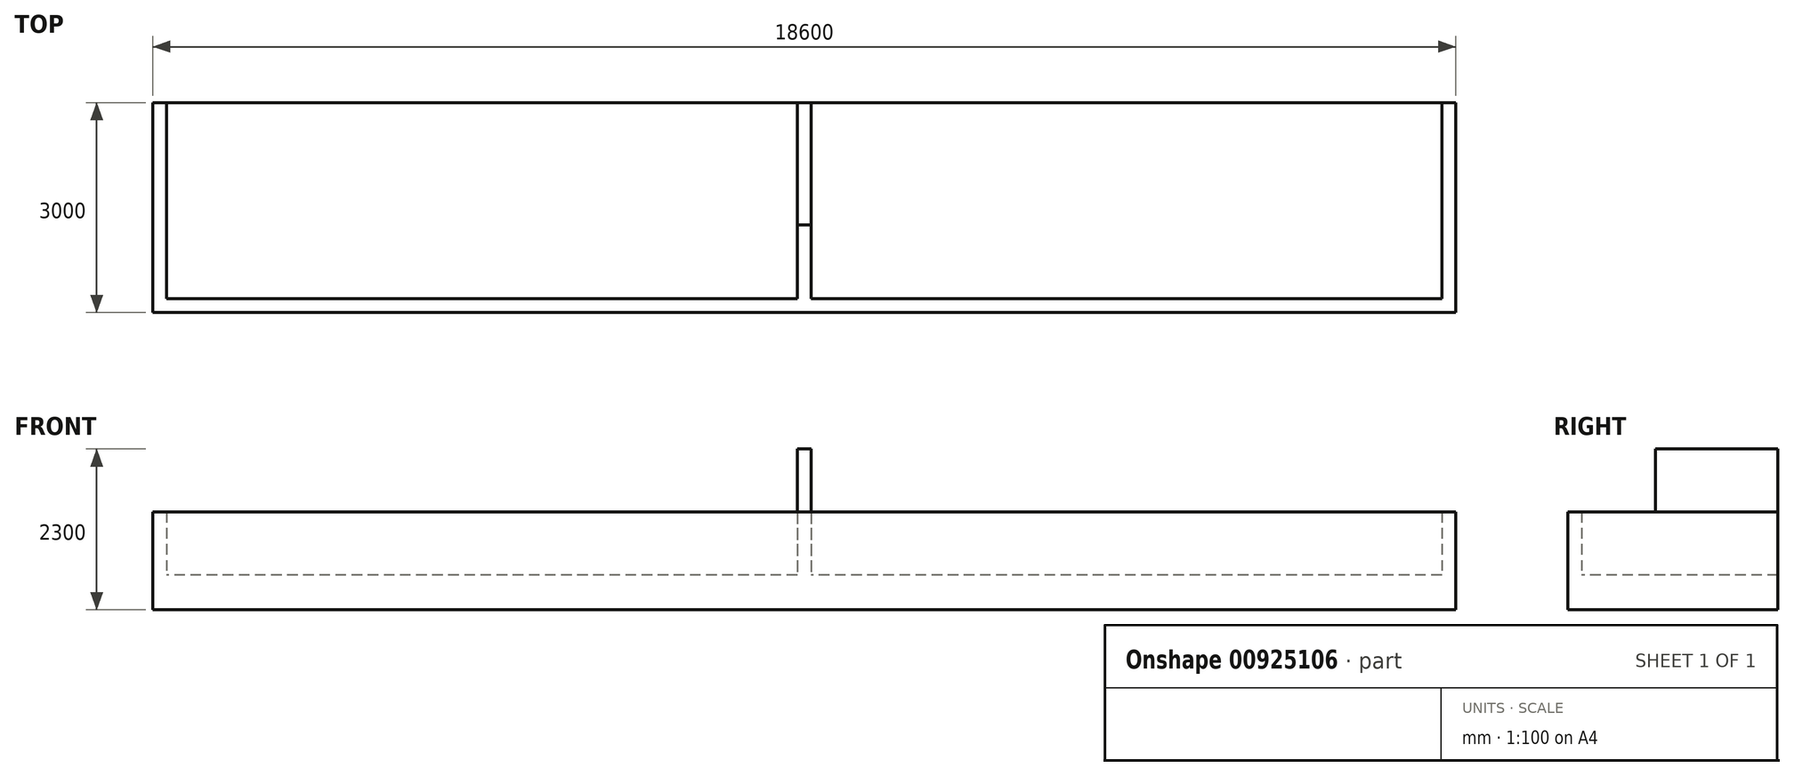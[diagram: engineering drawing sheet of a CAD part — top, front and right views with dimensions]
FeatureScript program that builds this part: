
annotation { "Feature Type Name" : "Feature", "Feature Type Description" : "" }
export const myFeature = defineFeature(function(context is Context, id is Id, definition is map)
    precondition{}
    {
        {
            var Q0;
            Q0=qCreatedBy(makeId("Top.planeOp"),FACE);
            var sketch = newSketch(context, id + "F0", { "sketchPlane" : qUnion([Q0])});
            skLineSegment(sketch, "E0.bottom", {"start": v(9300, 1500) * mm, "end": v(-9300, 1500) * mm});
            skLineSegment(sketch, "E0.top", {"start": v(9300, -1500) * mm, "end": v(-9300, -1500) * mm});
            skLineSegment(sketch, "E0.left", {"start": v(9300, 1500) * mm, "end": v(9300, -1500) * mm});
            skLineSegment(sketch, "E0.right", {"start": v(-9300, 1500) * mm, "end": v(-9300, -1500) * mm});
            skPoint(sketch, "E0.middle", {"position": v(0, 0) * mm});
            skLineSegment(sketch, "E1.bottom", {"start": v(-100, 1500) * mm, "end": v(100, 1500) * mm});
            skLineSegment(sketch, "E1.top", {"start": v(-100, -1500) * mm, "end": v(100, -1500) * mm});
            skLineSegment(sketch, "E1.left", {"start": v(-100, 1500) * mm, "end": v(-100, -1500) * mm});
            skLineSegment(sketch, "E1.right", {"start": v(100, 1500) * mm, "end": v(100, -1500) * mm});
            skLineSegment(sketch, "E2.top", {"start": v(-100, -250) * mm, "end": v(100, -250) * mm});
            skLineSegment(sketch, "E2.left", {"start": v(-100, -1500) * mm, "end": v(-100, -250) * mm});
            skLineSegment(sketch, "E2.right", {"start": v(100, -1500) * mm, "end": v(100, -250) * mm});
            skLineSegment(sketch, "E3.bottom", {"start": v(-9300, 1500) * mm, "end": v(-9100, 1500) * mm});
            skLineSegment(sketch, "E3.top", {"start": v(-9300, -1500) * mm, "end": v(-9100, -1500) * mm});
            skLineSegment(sketch, "E3.right", {"start": v(-9100, 1500) * mm, "end": v(-9100, -1500) * mm});
            skLineSegment(sketch, "E4.bottom", {"start": v(9300, 1500) * mm, "end": v(9100, 1500) * mm});
            skLineSegment(sketch, "E4.top", {"start": v(9300, -1500) * mm, "end": v(9100, -1500) * mm});
            skLineSegment(sketch, "E4.right", {"start": v(9100, 1500) * mm, "end": v(9100, -1500) * mm});
            skLineSegment(sketch, "E5.bottom", {"start": v(9100, -1500) * mm, "end": v(-9100, -1500) * mm});
            skLineSegment(sketch, "E5.top", {"start": v(9100, -1300) * mm, "end": v(-9100, -1300) * mm});
            skLineSegment(sketch, "E5.left", {"start": v(9100, -1500) * mm, "end": v(9100, -1300) * mm});
            skLineSegment(sketch, "E5.right", {"start": v(-9100, -1500) * mm, "end": v(-9100, -1300) * mm});
            skSolve(sketch);
        }
        {
            var Q0;
            {var subQ1=sQuery(id+"F0.wireOp",EDGE,"E0.bottom");var subQ5=sQuery(id+"F0.wireOp",EDGE,"E1.left");var subQ8=makeQuery(id+"F0.imprint","INTERSECT",VERTEX,{"derivedFrom":[subQ1,subQ5]});Q0=makeQuery(id+"F0.imprint","IMPRINT",FACE,{"disambiguationData":[TD([[makeQuery(id+"F0.imprint","IMPRINT",EDGE,{"disambiguationData":[TD([[subQ8,-1.0]])],"derivedFrom":subQ1}),1.0]])]});}
            var Q1;
            {var subQ0=sQuery(id+"F0.wireOp",EDGE,"E4.right");var subQ1=sQuery(id+"F0.wireOp",EDGE,"E0.bottom");var subQ2=makeQuery(id+"F0.imprint","INTERSECT",VERTEX,{"derivedFrom":[subQ1,subQ0]});Q1=makeQuery(id+"F0.imprint","IMPRINT",FACE,{"disambiguationData":[TD([[makeQuery(id+"F0.imprint","IMPRINT",EDGE,{"disambiguationData":[TD([[subQ2,-1.0]])],"derivedFrom":subQ1}),1.0]])]});}
            extrude(context, id + "F1", {"entities" : qUnion([Q0, Q1]), "depth" : 500 * mm, "offsetDistance" : 25 * mm});
        }
        {
            var Q0;
            {var subQ0=sQuery(id+"F0.wireOp",EDGE,"E0.right");Q0=makeQuery(id+"F0.imprint","IMPRINT",FACE,{"disambiguationData":[TD([[makeQuery(id+"F0.imprint","IMPRINT",EDGE,{"derivedFrom":subQ0}),1.0]])]});}
            var Q1;
            {var subQ0=sQuery(id+"F0.wireOp",EDGE,"E1.left");var subQ1=sQuery(id+"F0.wireOp",EDGE,"E0.top");var subQ2=makeQuery(id+"F0.imprint","INTERSECT",VERTEX,{"derivedFrom":[subQ1,subQ0]});Q1=makeQuery(id+"F0.imprint","IMPRINT",FACE,{"disambiguationData":[TD([[makeQuery(id+"F0.imprint","IMPRINT",EDGE,{"disambiguationData":[TD([[subQ2,-1.0]])],"derivedFrom":subQ1}),-1.0]])]});}
            var Q2;
            {var subQ4=sQuery(id+"F0.wireOp",EDGE,"E0.left");Q2=makeQuery(id+"F0.imprint","IMPRINT",FACE,{"disambiguationData":[TD([[makeQuery(id+"F0.imprint","IMPRINT",EDGE,{"derivedFrom":subQ4}),-1.0]])]});}
            var Q3;
            {var subQ0=sQuery(id+"F0.wireOp",EDGE,"E4.right");var subQ1=sQuery(id+"F0.wireOp",EDGE,"E0.top");var subQ2=makeQuery(id+"F0.imprint","INTERSECT",VERTEX,{"derivedFrom":[subQ1,subQ0]});Q3=makeQuery(id+"F0.imprint","IMPRINT",FACE,{"disambiguationData":[TD([[makeQuery(id+"F0.imprint","IMPRINT",EDGE,{"disambiguationData":[TD([[subQ2,-1.0]])],"derivedFrom":subQ1}),-1.0]])]});}
            var Q4;
            {var subQ0=sQuery(id+"F0.wireOp",EDGE,"E1.left");var subQ1=sQuery(id+"F0.wireOp",EDGE,"E0.top");var subQ2=makeQuery(id+"F0.imprint","INTERSECT",VERTEX,{"derivedFrom":[subQ1,subQ0]});Q4=makeQuery(id+"F0.imprint","IMPRINT",FACE,{"disambiguationData":[TD([[makeQuery(id+"F0.imprint","IMPRINT",EDGE,{"disambiguationData":[TD([[subQ2,1.0]])],"derivedFrom":subQ1}),-1.0]])]});}
            var Q5;
            {var subQ0=sQuery(id+"F0.wireOp",EDGE,"E2.top");Q5=makeQuery(id+"F0.imprint","IMPRINT",FACE,{"disambiguationData":[TD([[makeQuery(id+"F0.imprint","IMPRINT",EDGE,{"derivedFrom":subQ0}),-1.0]])]});}
            extrude(context, id + "F2", {"entities" : qUnion([Q0, Q1, Q2, Q3, Q4, Q5]), "depth" : 1400 * mm, "offsetDistance" : 25 * mm});
        }
        {
            var Q0;
            {var subQ5=sQuery(id+"F0.wireOp",EDGE,"E2.top");Q0=makeQuery(id+"F0.imprint","IMPRINT",FACE,{"disambiguationData":[TD([[makeQuery(id+"F0.imprint","IMPRINT",EDGE,{"derivedFrom":subQ5}),1.0]])]});}
            extrude(context, id + "F3", {"entities" : qUnion([Q0]), "operationType" : NewBodyOperationType.ADD, "depth" : 2300 * mm, "offsetDistance" : 25 * mm});
        }
    });
